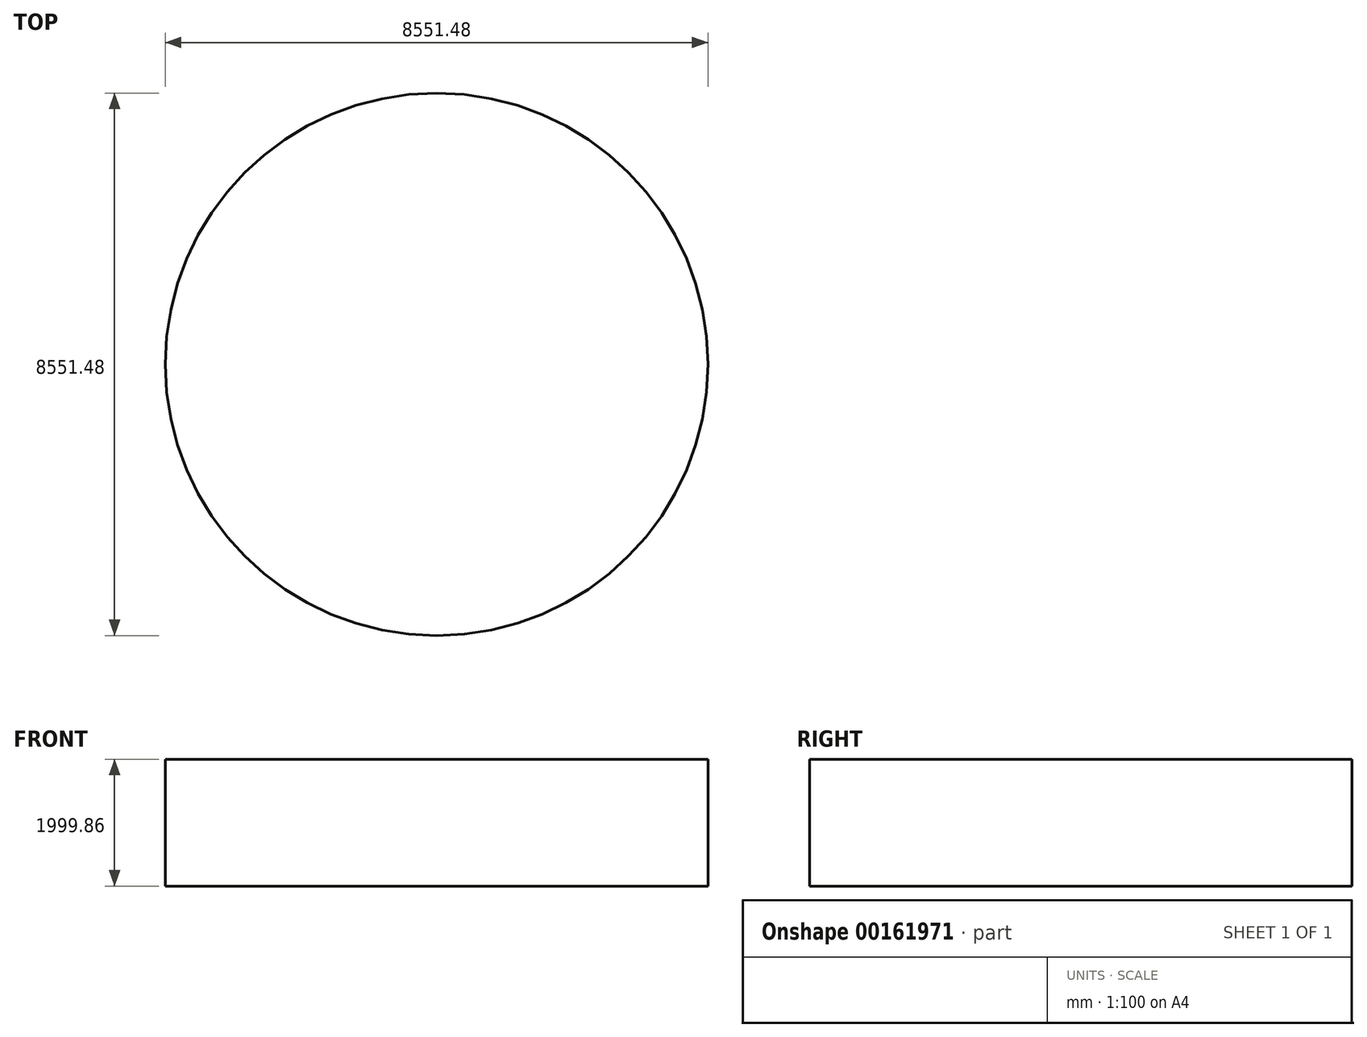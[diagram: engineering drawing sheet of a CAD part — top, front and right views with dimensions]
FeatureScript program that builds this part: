
annotation { "Feature Type Name" : "Feature", "Feature Type Description" : "" }
export const myFeature = defineFeature(function(context is Context, id is Id, definition is map)
    precondition{}
    {
        {
            var Q0;
            Q0=qCreatedBy(makeId("Front.planeOp"),FACE);
            var sketch = newSketch(context, id + "F0", { "sketchPlane" : qUnion([Q0])});
            skLineSegment(sketch, "E0", {"start": v(0, 3545.5) * mm, "end": v(0, -2909.03) * mm, "construction": true});
            skLineSegment(sketch, "E1", {"start": v(0, 0) * mm, "end": v(-5000, 0) * mm});
            skLineSegment(sketch, "E2", {"start": v(-5000, 0) * mm, "end": v(-5000, 2419.35) * mm});
            skLineSegment(sketch, "E3", {"start": v(-5000, 2419.35) * mm, "end": v(0, 2419.35) * mm});
            skSolve(sketch);
        }
        {
            var Q0;
            Q0=qCreatedBy(makeId("Front.planeOp"),FACE);
            var sketch = newSketch(context, id + "F1", { "sketchPlane" : qUnion([Q0])});
            skLineSegment(sketch, "E4", {"start": v(0, 0) * mm, "end": v(0, 1999.86) * mm});
            skLineSegment(sketch, "E5", {"start": v(0, 1999.86) * mm, "end": v(-4275.74, 1999.86) * mm});
            skLineSegment(sketch, "E6", {"start": v(-4275.74, 1999.86) * mm, "end": v(-4275.74, 0) * mm});
            skLineSegment(sketch, "E7", {"start": v(-4275.74, 0) * mm, "end": v(0, 0) * mm});
            skSolve(sketch);
        }
        {
            var Q0;
            Q0=makeQuery(id+"F1.imprint","IMPRINT",FACE,{"disambiguationData":[TD([[makeQuery(id+"F1.imprint","IMPRINT",EDGE,{"derivedFrom":sQuery(id+"F1.wireOp",EDGE,"E4")}),1.0]])]});
            var Q1;
            Q1=sQuery(id+"F0.wireOp",EDGE,"E0");
            revolve(context, id + "F2", {"surfaceOperationType" : NewSurfaceOperationType.NEW, "entities" : qUnion([Q0]), "axis" : qUnion([Q1]), "revolveType" : RevolveType.FULL});
        }
    });
